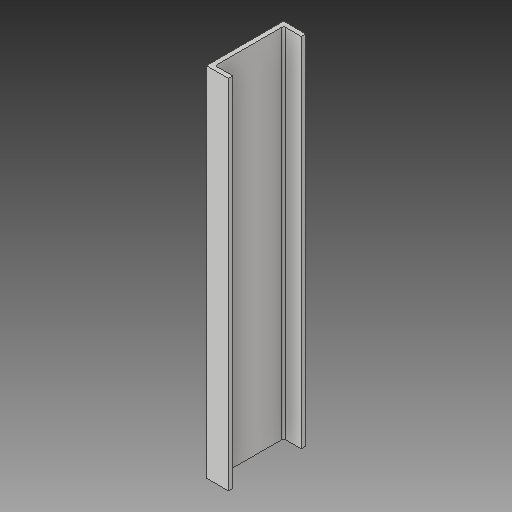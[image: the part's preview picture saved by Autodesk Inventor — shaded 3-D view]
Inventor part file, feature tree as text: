
AUTODESK INVENTOR PART (.ipt)
format: ipt  version: 2019 (Build 230136000, 136)  size: 103,424 bytes
history: native  units: in
note: dims shown in document units (in); Inventor stores cm internally (conversion verified against a paired STEP export)
features: other x3, sketch x3
ambient origin geometry x8: Origin, YZ Plane, XZ Plane, XY Plane, X Axis, Y Axis, Z Axis, Center Point
bodies: Solid1 (feature_tree)
feature tree (6):
  other  "Base1.ipt"
  other  "Solid1::Base1.ipt"
  other  "TaggingFeature1"
  sketch  "Sketch1"  dims[d0=0.3937in]
  sketch  "Sketch2"
  sketch  "Sketch3"
